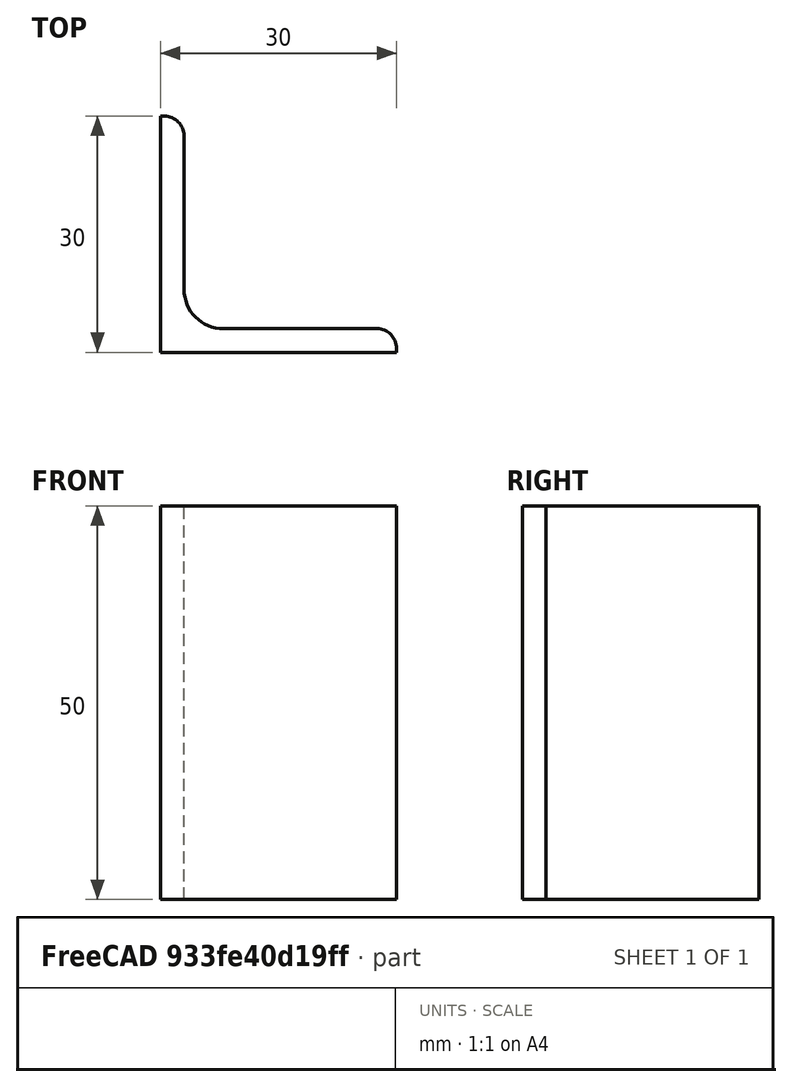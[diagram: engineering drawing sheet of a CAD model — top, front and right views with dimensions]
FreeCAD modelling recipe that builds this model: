
FCSTD DOCUMENT  (FreeCAD 0.15R4671 (Git))
Label: Angle Bar L30x30x3 EN10056 S235JR
License: All rights reserved
LicenseURL: http://en.wikipedia.org/wiki/All_rights_reserved
objects: Sketcher::SketchObject×1, Part::Extrusion×1
note: 2 computed .brp shape members not serialized (recipe doc carries the construction recipe); baked Part::Feature solids carry a one-line shape summary decoded from their .brp

FEATURE [Sketcher::SketchObject] Sketch
  sketch-geometry (9):
    g0: LineSegment StartX=0 StartY=0 StartZ=0 EndX=30 EndY=0 EndZ=0
    g1: LineSegment StartX=30 StartY=0 StartZ=0 EndX=30 EndY=0.5 EndZ=0
    g2: LineSegment StartX=27.5 StartY=3 StartZ=0 EndX=8 EndY=3 EndZ=0
    g3: LineSegment StartX=0 StartY=0 StartZ=0 EndX=0 EndY=30 EndZ=0
    g4: LineSegment StartX=0 StartY=30 StartZ=0 EndX=0.5 EndY=30 EndZ=0
    g5: LineSegment StartX=3 StartY=27.5 StartZ=0 EndX=3 EndY=8 EndZ=0
    g6: ArcOfCircle CenterX=8 CenterY=8 CenterZ=0 NormalX=0 NormalY=0 NormalZ=1 Radius=5 StartAngle=3.14159 EndAngle=4.71239
    g7: ArcOfCircle CenterX=0.5 CenterY=27.5 CenterZ=0 NormalX=0 NormalY=0 NormalZ=1 Radius=2.5 StartAngle=0 EndAngle=1.5708
    g8: ArcOfCircle CenterX=27.5 CenterY=0.5 CenterZ=0 NormalX=0 NormalY=0 NormalZ=1 Radius=2.5 StartAngle=0 EndAngle=1.5708
  constraints (23):
    c: Coincident(g0,g-1)
    c: Horizontal(g0)
    c: Coincident(g1,g0)
    c: Vertical(g1)
    c: Horizontal(g2)
    c: Coincident(g3,g-1)
    c: Vertical(g3)
    c: Coincident(g4,g3)
    c: Horizontal(g4)
    c: Vertical(g5)
    c: Tangent(g5,g6) = -1.5708
    c: Tangent(g2,g6) = 1.5708
    c: Tangent(g4,g7) = 1.5708
    c: Tangent(g5,g7) = 1.5708
    c: Tangent(g2,g8) = -1.5708
    c: Tangent(g1,g8) = -1.5708
    c: DistanceX(g0) = 30
    c: DistanceY(g3) = 30
    c: DistanceY(g0,g2) = 3
    c: DistanceX(g3,g5) = 3
    c: Radius(g6) = 5
    c: Radius(g8) = 2.5
    c: Radius(g7) = 2.5
FEATURE [Part::Extrusion] Extrude  label="Angle Bar L30x30x3 EN10056 S235JR"
  Base = -> Sketch
  Dir = (0,0,50)
  Solid = true
